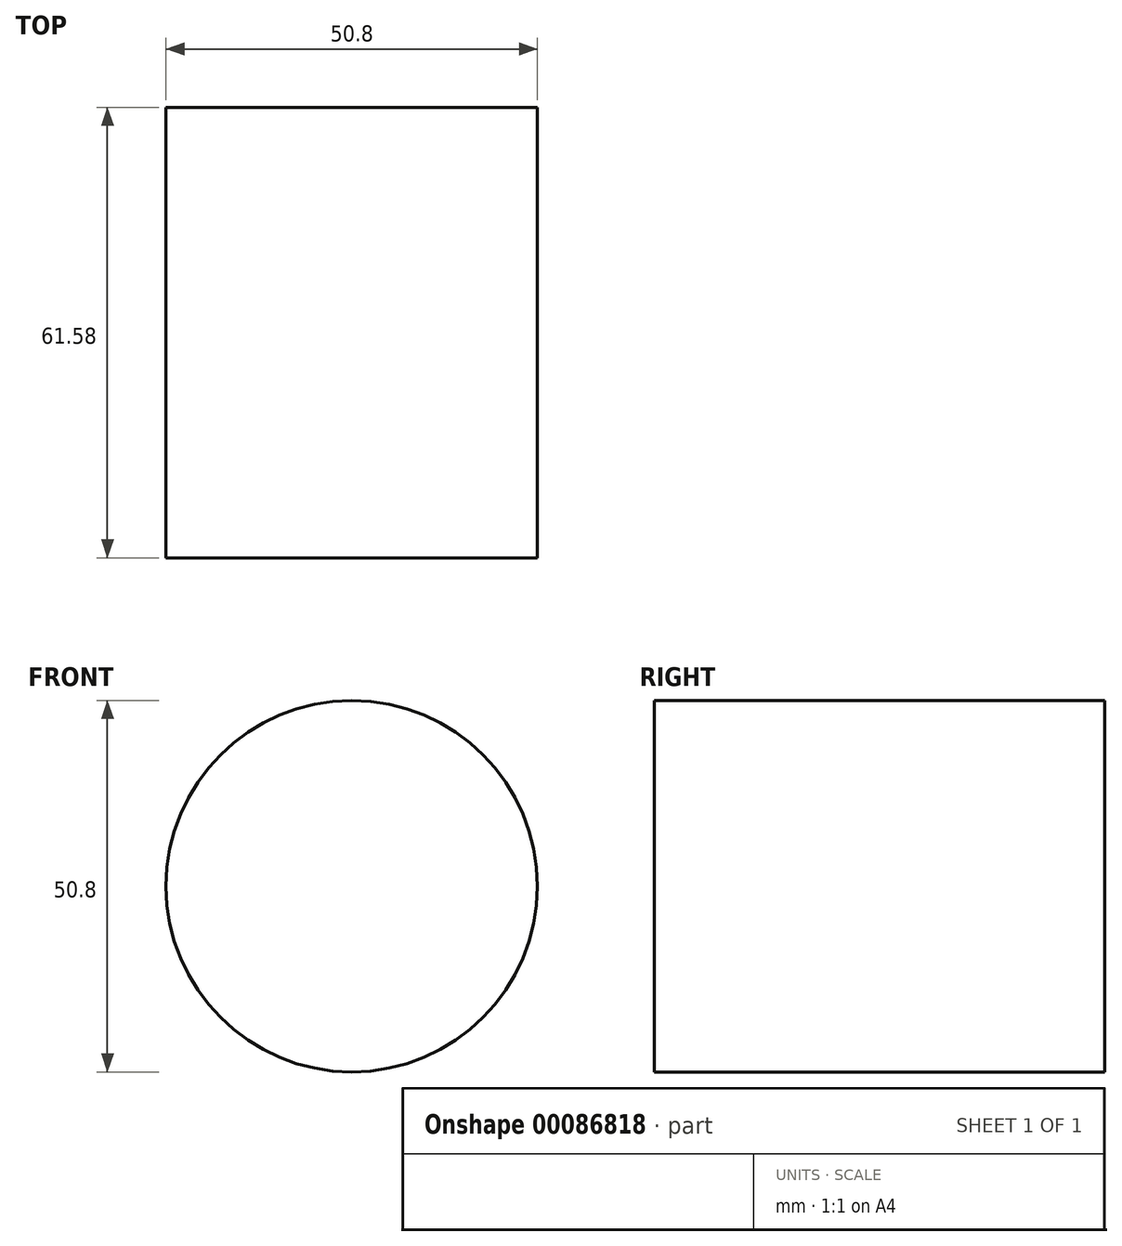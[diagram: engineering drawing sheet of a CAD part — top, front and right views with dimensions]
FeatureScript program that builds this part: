
annotation { "Feature Type Name" : "Feature", "Feature Type Description" : "" }
export const myFeature = defineFeature(function(context is Context, id is Id, definition is map)
    precondition{}
    {
        {
            var Q0;
            Q0=qCreatedBy(makeId("Front.planeOp"),FACE);
            var sketch = newSketch(context, id + "F0", { "sketchPlane" : qUnion([Q0])});
            skCircle(sketch, "E0", {"center": v(0, 0) * mm, "radius": 25.4 * mm});
            skSolve(sketch);
        }
        {
            var Q0;
            Q0 = qSketchRegion(id + "F0", true);
            extrude(context, id + "F1", {"entities" : qUnion([Q0]), "depth" : 61.58 * mm});
        }
    });
